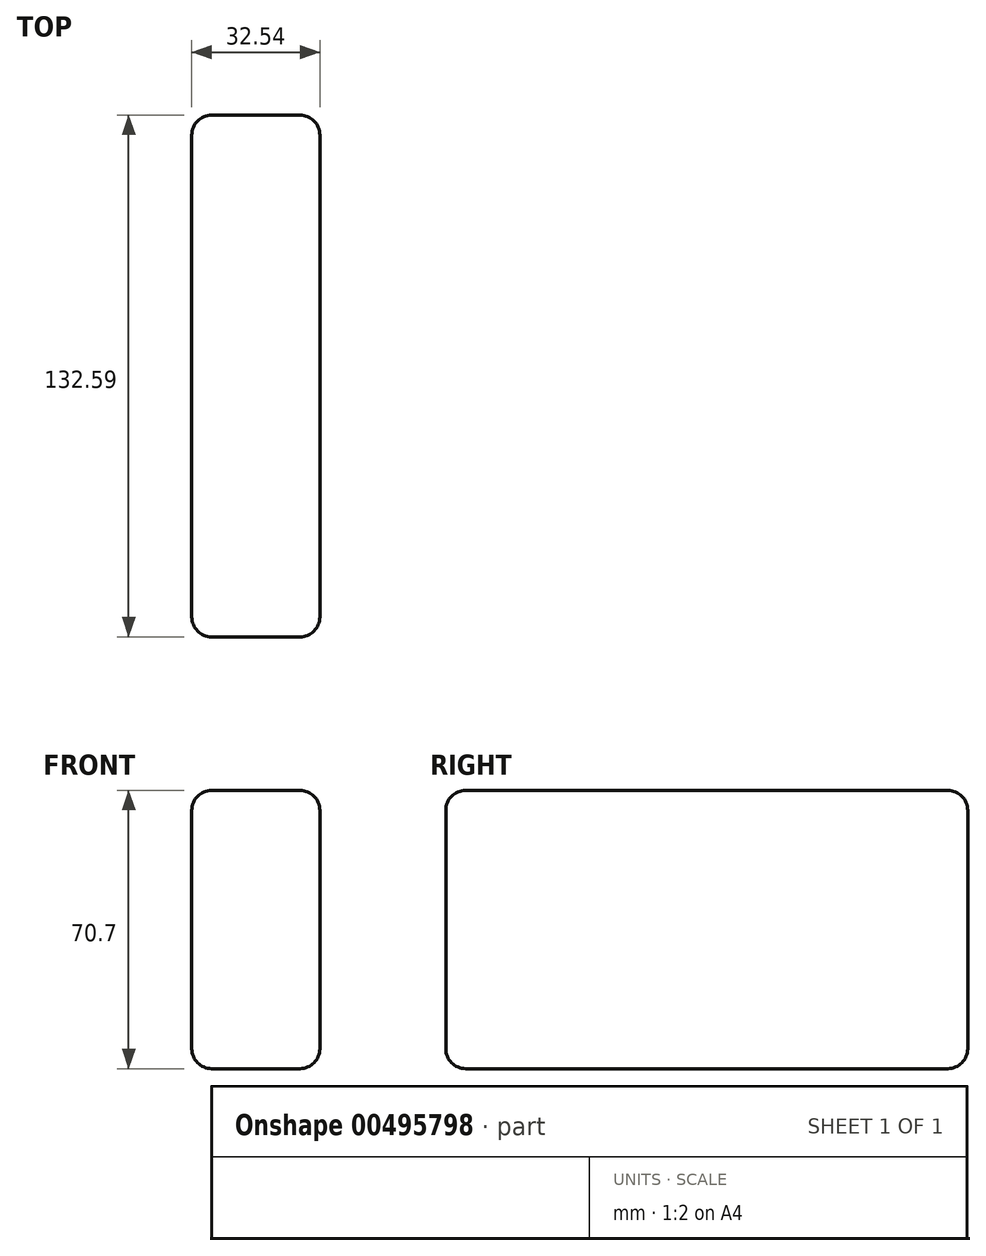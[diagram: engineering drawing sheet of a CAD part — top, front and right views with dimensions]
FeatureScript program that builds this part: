
annotation { "Feature Type Name" : "Feature", "Feature Type Description" : "" }
export const myFeature = defineFeature(function(context is Context, id is Id, definition is map)
    precondition{}
    {
        {
            var Q0;
            Q0=qCreatedBy(makeId("Front.planeOp"),FACE);
            var sketch = newSketch(context, id + "F0", { "sketchPlane" : qUnion([Q0])});
            skLineSegment(sketch, "E0.bottom", {"start": v(-140.4, 70.7) * mm, "end": v(-60.36, 70.7) * mm});
            skLineSegment(sketch, "E0.top", {"start": v(-140.4, 0) * mm, "end": v(-60.36, 0) * mm});
            skLineSegment(sketch, "E0.left", {"start": v(-140.4, 70.7) * mm, "end": v(-140.4, 0) * mm});
            skLineSegment(sketch, "E0.right", {"start": v(-60.36, 70.7) * mm, "end": v(-60.36, 0) * mm});
            skSolve(sketch);
        }
        {
            var Q0;
            Q0 = qSketchRegion(id + "F0", true);
            extrude(context, id + "F1", {"entities" : qUnion([Q0]), "depth" : 132.6 * mm});
        }
        {
            var Q0;
            Q0=makeQuery(id+"F1.opExtrude","SWEPT_FACE",FACE,{"disambiguationData":[OSD([sQuery(id+"F0.wireOp",EDGE,"E0.right")])]});
            extrude(context, id + "F2", {"entities" : qUnion([Q0]), "operationType" : NewBodyOperationType.ADD, "oppositeDirection" : true, "depth" : 48 * mm});
        }
        {
            var Q0;
            Q0=makeQuery(id+"F1.opExtrude","SWEPT_FACE",FACE,{"disambiguationData":[OSD([sQuery(id+"F0.wireOp",EDGE,"E0.right")])]});
            extrude(context, id + "F3", {"entities" : qUnion([Q0]), "operationType" : NewBodyOperationType.REMOVE, "oppositeDirection" : true, "depth" : 47.5 * mm});
        }
        {
            var Q0;
            Q0=makeQuery(id+"F3.boolean.opBoolean","COPY",EDGE,{"derivedFrom":makeQuery(id+"F3.opExtrude","CAP_EDGE",EDGE,{"disambiguationData":[OSD([sQuery(id+"F0.wireOp",EDGE,"E0.bottom"),sQuery(id+"F0.wireOp",EDGE,"E0.right")])],"isStart":false})});
            var Q1;
            Q1=makeQuery(id+"F1.opExtrude","CAP_EDGE",EDGE,{"disambiguationData":[OSD([sQuery(id+"F0.wireOp",EDGE,"E0.bottom")])],"isStart":false});
            var Q2;
            Q2=makeQuery(id+"F1.opExtrude","SWEPT_EDGE",EDGE,{"disambiguationData":[OSD([sQuery(id+"F0.wireOp",EDGE,"E0.bottom"),sQuery(id+"F0.wireOp",EDGE,"E0.left")])]});
            var Q3;
            Q3=makeQuery(id+"F1.opExtrude","CAP_EDGE",EDGE,{"disambiguationData":[OSD([sQuery(id+"F0.wireOp",EDGE,"E0.bottom")])],"isStart":true});
            var Q4;
            {var subQ0=sQuery(id+"F0.wireOp",EDGE,"E0.right");Q4=makeQuery(id+"F3.boolean.opBoolean","COPY",EDGE,{"derivedFrom":makeQuery(id+"F3.opExtrude","CAP_EDGE",EDGE,{"disambiguationData":[OSD([subQ0]),TDD([makeQuery(id+"F1.opExtrude","CAP_EDGE",EDGE,{"disambiguationData":[OSD([subQ0])],"isStart":false})])],"isStart":false})});}
            var Q5;
            Q5=makeQuery(id+"F1.opExtrude","CAP_EDGE",EDGE,{"disambiguationData":[OSD([sQuery(id+"F0.wireOp",EDGE,"E0.top")])],"isStart":false});
            var Q6;
            {var subQ0=sQuery(id+"F0.wireOp",EDGE,"E0.right");Q6=makeQuery(id+"F3.boolean.opBoolean","COPY",EDGE,{"derivedFrom":makeQuery(id+"F3.opExtrude","CAP_EDGE",EDGE,{"disambiguationData":[OSD([subQ0]),TDD([makeQuery(id+"F1.opExtrude","CAP_EDGE",EDGE,{"disambiguationData":[OSD([subQ0])],"isStart":true})])],"isStart":false})});}
            var Q7;
            Q7=makeQuery(id+"F3.boolean.opBoolean","COPY",FACE,{"derivedFrom":makeQuery(id+"F3.opExtrude","CAP_FACE",FACE,{"disambiguationData":[OSD([sQuery(id+"F0.wireOp",EDGE,"E0.right")])],"isStart":false})});
            var Q8;
            Q8=makeQuery(id+"F1.opExtrude","CAP_EDGE",EDGE,{"disambiguationData":[OSD([sQuery(id+"F0.wireOp",EDGE,"E0.top")])],"isStart":true});
            var Q9;
            Q9=makeQuery(id+"F1.opExtrude","CAP_EDGE",EDGE,{"disambiguationData":[OSD([sQuery(id+"F0.wireOp",EDGE,"E0.left")])],"isStart":true});
            var Q10;
            Q10=makeQuery(id+"F1.opExtrude","SWEPT_EDGE",EDGE,{"disambiguationData":[OSD([sQuery(id+"F0.wireOp",EDGE,"E0.top"),sQuery(id+"F0.wireOp",EDGE,"E0.left")])]});
            fillet(context, id + "F4", {"entities" : qUnion([Q0, Q1, Q2, Q3, Q4, Q5, Q6, Q7, Q8, Q9, Q10]), "radius" : 5.08 * mm, "tangentPropagation" : true, "allowEdgeOverflow" : false});
        }
        {
            var Q0;
            Q0=makeQuery(id+"F1.opExtrude","SWEPT_FACE",FACE,{"disambiguationData":[OSD([sQuery(id+"F0.wireOp",EDGE,"E0.left")])]});
            fillet(context, id + "F5", {"entities" : qUnion([Q0]), "radius" : 5.08 * mm, "tangentPropagation" : true, "allowEdgeOverflow" : false});
        }
    });
